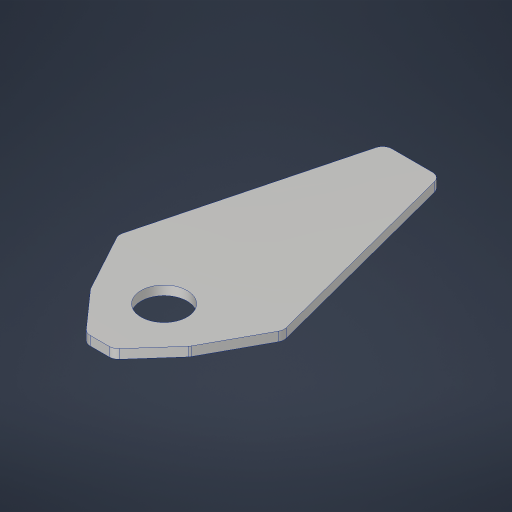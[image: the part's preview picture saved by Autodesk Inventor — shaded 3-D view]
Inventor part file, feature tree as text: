
AUTODESK INVENTOR PART (.ipt)
format: ipt  version: 2023.4 (Build 274418000, 418)  size: 205,312 bytes
history: native  units: in
note: dims shown in document units (in); Inventor stores cm internally (conversion verified against a paired STEP export)
features: fillet x3, sketch x2, extrude x1, hole x1, chamfer x1, projected_geometry x1
ambient origin geometry x8: Origin, YZ Plane, XZ Plane, XY Plane, X Axis, Y Axis, Z Axis, Center Point
bodies: Solid1 (feature_tree)
feature tree (9):
  extrude  "Extrusion1"  Depth=0.25in
  fillet  "Fillet1"  Radius=0.25in
  fillet  "Fillet2"  Radius=4.5in
  hole  "Hole1"  [1 undecoded]
  chamfer  "Chamfer1"  Distance=1.5in
  fillet  "Fillet3"  Radius=0.25in
  sketch  "Sketch1"  dims[d0=1.0in d1=2.0in d2=0.25in d3=4.5in]
  sketch  "Sketch2"  dims[d4=8.5in d5=0.75in d6=1.5in d7=0.25in d8=0.0in d9=0.26in d10=1.0in d11=1.25in d12=0.75in d13=0.332in d14=0.25in d15=0.5635in d16=1.0in d17=0.8108in d20=0.375in d21=1.25in d22=45.0deg d23=0.26in]
  projected_geometry  "Project Cut Edges1"
note: 1 required parameter value undecoded (feature->parameter linkage not recoverable at this tier; creation-order binding heuristic only, values carry confidence <= 0.55)
